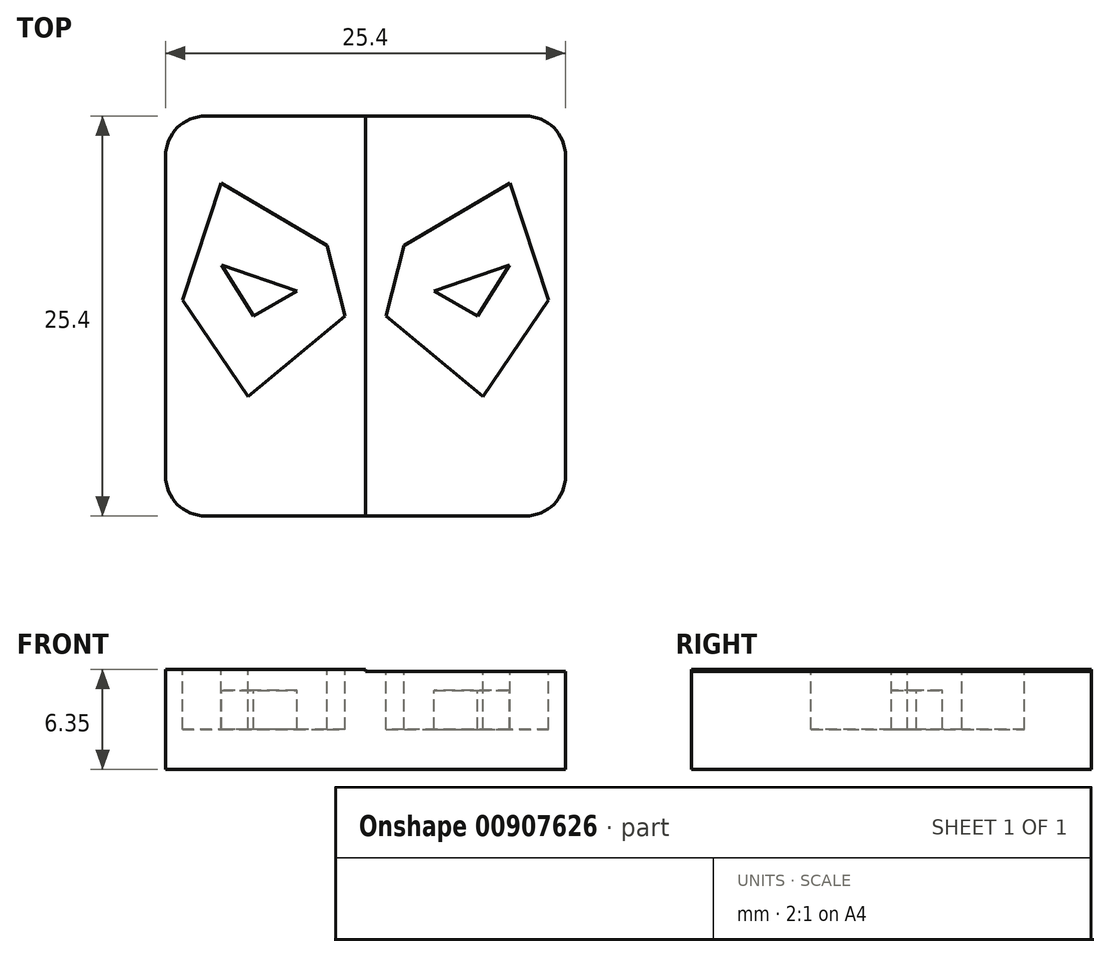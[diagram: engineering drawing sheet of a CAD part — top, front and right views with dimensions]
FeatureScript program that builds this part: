
annotation { "Feature Type Name" : "Feature", "Feature Type Description" : "" }
export const myFeature = defineFeature(function(context is Context, id is Id, definition is map)
    precondition{}
    {
        {
            var Q0;
            Q0=qCreatedBy(makeId("Top.planeOp"),FACE);
            var sketch = newSketch(context, id + "F0", { "sketchPlane" : qUnion([Q0])});
            skLineSegment(sketch, "E0.bottom", {"start": v(-10.16, 12.7) * mm, "end": v(10.16, 12.7) * mm});
            skLineSegment(sketch, "E0.top", {"start": v(-10.16, -12.7) * mm, "end": v(10.16, -12.7) * mm});
            skLineSegment(sketch, "E0.left", {"start": v(-12.7, 10.16) * mm, "end": v(-12.7, -10.16) * mm});
            skLineSegment(sketch, "E0.right", {"start": v(12.7, 10.16) * mm, "end": v(12.7, -10.16) * mm});
            skPoint(sketch, "E0.middle", {"position": v(0, 0) * mm});
            skLineSegment(sketch, "E1", {"start": v(1.31, 0) * mm, "end": v(7.47, -5.1) * mm});
            skLineSegment(sketch, "E2", {"start": v(7.47, -5.1) * mm, "end": v(11.63, 1.03) * mm});
            skLineSegment(sketch, "E3", {"start": v(11.63, 1.03) * mm, "end": v(9.17, 8.46) * mm});
            skLineSegment(sketch, "E4", {"start": v(9.17, 8.46) * mm, "end": v(2.43, 4.48) * mm});
            skLineSegment(sketch, "E5", {"start": v(2.43, 4.48) * mm, "end": v(1.31, 0) * mm});
            skLineSegment(sketch, "E6", {"start": v(9.15, 3.23) * mm, "end": v(4.34, 1.58) * mm});
            skLineSegment(sketch, "E7", {"start": v(4.34, 1.58) * mm, "end": v(7.12, 0) * mm});
            skLineSegment(sketch, "E8", {"start": v(7.12, 0) * mm, "end": v(9.15, 3.23) * mm});
            skPoint(sketch, "E9.visualSharp", {"position": v(-12.7, 12.7) * mm});
            skPoint(sketch, "E10.visualSharp", {"position": v(12.7, 12.7) * mm});
            skArc(sketch, "E10.filletArc", {"start": v(12.7, 10.16) * mm, "mid": v(11.96, 11.96) * mm, "end": v(10.16, 12.7) * mm});
            skPoint(sketch, "E11.visualSharp", {"position": v(12.7, -12.7) * mm});
            skLineSegment(sketch, "E11.filletArc", {"start": v(12.7, -12.7) * mm, "end": v(12.7, -12.7) * mm});
            skPoint(sketch, "E12.visualSharp", {"position": v(-12.7, -12.7) * mm});
            skArc(sketch, "E12.filletArc", {"start": v(-12.7, -10.16) * mm, "mid": v(-11.96, -11.96) * mm, "end": v(-10.16, -12.7) * mm});
            skArc(sketch, "E13.filletArc", {"start": v(-10.16, 12.7) * mm, "mid": v(-11.96, 11.96) * mm, "end": v(-12.7, 10.16) * mm});
            skArc(sketch, "E14.filletArc", {"start": v(10.16, -12.7) * mm, "mid": v(11.96, -11.96) * mm, "end": v(12.7, -10.16) * mm});
            skLineSegment(sketch, "E15.MirrorCS", {"start": v(-2.43, 4.48) * mm, "end": v(-1.31, 0) * mm});
            skLineSegment(sketch, "E16.MirrorCS", {"start": v(-7.12, 0) * mm, "end": v(-9.15, 3.23) * mm});
            skLineSegment(sketch, "E17.MirrorCS", {"start": v(-7.47, -5.1) * mm, "end": v(-11.63, 1.03) * mm});
            skLineSegment(sketch, "E18.MirrorCS", {"start": v(-11.63, 1.03) * mm, "end": v(-9.17, 8.46) * mm});
            skLineSegment(sketch, "E19.MirrorCS", {"start": v(-4.34, 1.58) * mm, "end": v(-7.12, 0) * mm});
            skLineSegment(sketch, "E20.MirrorCS", {"start": v(-9.17, 8.46) * mm, "end": v(-2.43, 4.48) * mm});
            skLineSegment(sketch, "E21.MirrorCS", {"start": v(-1.31, 0) * mm, "end": v(-7.47, -5.1) * mm});
            skLineSegment(sketch, "E22.MirrorCS", {"start": v(-9.15, 3.23) * mm, "end": v(-4.34, 1.58) * mm});
            skLineSegment(sketch, "E23", {"start": v(0, 12.7) * mm, "end": v(0, -12.7) * mm});
            skSolve(sketch);
        }
        {
            var Q0;
            Q0=makeQuery(id+"F0.imprint","IMPRINT",FACE,{"disambiguationData":[TD([[makeQuery(id+"F0.imprint","IMPRINT",EDGE,{"derivedFrom":sQuery(id+"F0.wireOp",EDGE,"E0.bottom")}),-1.0]])]});
            var Q1;
            Q1=makeQuery(id+"F0.imprint","IMPRINT",FACE,{"disambiguationData":[TD([[makeQuery(id+"F0.imprint","IMPRINT",EDGE,{"derivedFrom":sQuery(id+"F0.wireOp",EDGE,"E15.MirrorCS")}),-1.0]])]});
            var Q2;
            Q2=makeQuery(id+"F0.imprint","IMPRINT",FACE,{"disambiguationData":[TD([[makeQuery(id+"F0.imprint","IMPRINT",EDGE,{"derivedFrom":sQuery(id+"F0.wireOp",EDGE,"E16.MirrorCS")}),-1.0]])]});
            var Q3;
            Q3=makeQuery(id+"F0.imprint","IMPRINT",FACE,{"disambiguationData":[TD([[makeQuery(id+"F0.imprint","IMPRINT",EDGE,{"derivedFrom":sQuery(id+"F0.wireOp",EDGE,"E1")}),1.0]])]});
            var Q4;
            Q4=makeQuery(id+"F0.imprint","IMPRINT",FACE,{"disambiguationData":[TD([[makeQuery(id+"F0.imprint","IMPRINT",EDGE,{"derivedFrom":sQuery(id+"F0.wireOp",EDGE,"E6")}),1.0]])]});
            extrude(context, id + "F1", {"entities" : qUnion([Q0, Q1, Q2, Q3, Q4]), "oppositeDirection" : true, "depth" : 6.35 * mm, "offsetDistance" : 25.4 * mm});
        }
        {
            var Q0;
            Q0=makeQuery(id+"F0.imprint","IMPRINT",FACE,{"disambiguationData":[TD([[makeQuery(id+"F0.imprint","IMPRINT",EDGE,{"derivedFrom":sQuery(id+"F0.wireOp",EDGE,"E15.MirrorCS")}),-1.0]])]});
            var Q1;
            Q1=makeQuery(id+"F0.imprint","IMPRINT",FACE,{"disambiguationData":[TD([[makeQuery(id+"F0.imprint","IMPRINT",EDGE,{"derivedFrom":sQuery(id+"F0.wireOp",EDGE,"E1")}),1.0]])]});
            extrude(context, id + "F2", {"entities" : qUnion([Q0, Q1]), "operationType" : NewBodyOperationType.REMOVE, "oppositeDirection" : true, "depth" : 3.8 * mm, "offsetDistance" : 25.4 * mm});
        }
        {
            var Q0;
            Q0=makeQuery(id+"F0.imprint","IMPRINT",FACE,{"disambiguationData":[TD([[makeQuery(id+"F0.imprint","IMPRINT",EDGE,{"derivedFrom":sQuery(id+"F0.wireOp",EDGE,"E16.MirrorCS")}),-1.0]])]});
            var Q1;
            Q1=makeQuery(id+"F0.imprint","IMPRINT",FACE,{"disambiguationData":[TD([[makeQuery(id+"F0.imprint","IMPRINT",EDGE,{"derivedFrom":sQuery(id+"F0.wireOp",EDGE,"E6")}),1.0]])]});
            extrude(context, id + "F3", {"entities" : qUnion([Q0, Q1]), "operationType" : NewBodyOperationType.REMOVE, "oppositeDirection" : true, "depth" : 1.32 * mm, "offsetDistance" : 25.4 * mm});
        }
        {
            var Q0;
            Q0=makeQuery(id+"F0.imprint","IMPRINT",FACE,{"disambiguationData":[TD([[makeQuery(id+"F0.imprint","IMPRINT",EDGE,{"derivedFrom":sQuery(id+"F0.wireOp",EDGE,"E0.right")}),-1.0]])]});
            extrude(context, id + "F4", {"entities" : qUnion([Q0]), "operationType" : NewBodyOperationType.REMOVE, "oppositeDirection" : true, "depth" : 0.13 * mm, "offsetDistance" : 25.4 * mm});
        }
    });
